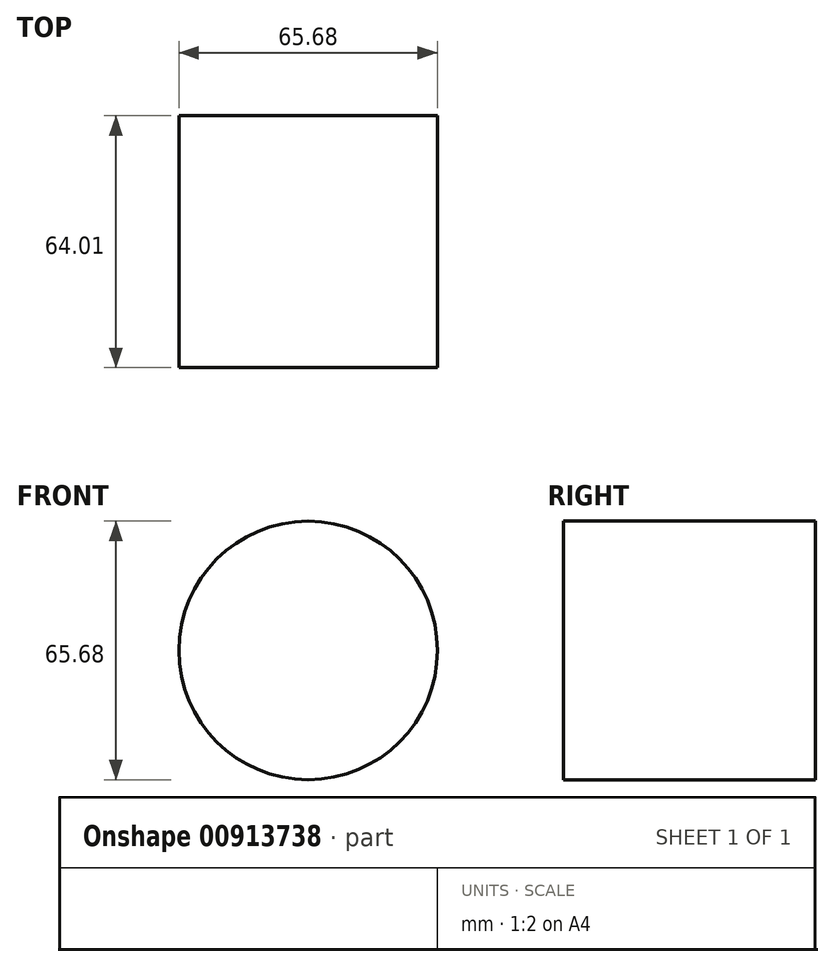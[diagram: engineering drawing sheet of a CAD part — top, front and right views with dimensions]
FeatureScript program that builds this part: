
annotation { "Feature Type Name" : "Feature", "Feature Type Description" : "" }
export const myFeature = defineFeature(function(context is Context, id is Id, definition is map)
    precondition{}
    {
        {
            var Q0;
            Q0=qCreatedBy(makeId("Front.planeOp"),FACE);
            var sketch = newSketch(context, id + "F0", { "sketchPlane" : qUnion([Q0])});
            skCircle(sketch, "E0", {"center": v(0, 0) * mm, "radius": 32.84 * mm});
            skSolve(sketch);
        }
        {
            var Q0;
            Q0 = qSketchRegion(id + "F0", true);
            extrude(context, id + "F1", {"entities" : qUnion([Q0]), "depth" : 64 * mm, "offsetDistance" : 25.4 * mm});
        }
    });
